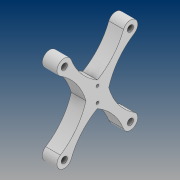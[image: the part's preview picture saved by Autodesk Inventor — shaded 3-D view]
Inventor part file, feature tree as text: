
AUTODESK INVENTOR PART (.ipt)
format: ipt  version: 2021 (Build 250183000, 183)  size: 144,384 bytes
history: native  units: mm
features: sketch x3, hole x2, extrude x1, projected_geometry x1
ambient origin geometry x8: Origin, YZ Plane, XZ Plane, XY Plane, X Axis, Y Axis, Z Axis, Center Point
bodies: Solid1 (feature_tree)
feature tree (7):
  extrude  "Extrusion1"  Depth=45.0mm
  hole  "Hole1"  [1 undecoded]
  hole  "Hole2"  [1 undecoded]
  sketch  "Sketch1"  dims[d0=55.0mm d1=45.0mm]
  sketch  "Sketch2"  dims[d2=10.0mm d3=15.0mm]
  projected_geometry  "Projected Loop1"
  sketch  "Sketch3"  dims[d4=41.0mm d5=10.0mm d6=0.0mm d7=4.2mm d8=6.0mm d9=4.0mm d10=2.0mm d11=90.0deg d12=8.0mm d13=20.594885mm d14=10.0mm d15=1.8mm d16=6.0mm d17=4.0mm d18=2.0mm d19=90.0deg d20=8.0mm d21=20.594885mm]
note: 2 required parameter values undecoded (feature->parameter linkage not recoverable at this tier; creation-order binding heuristic only, values carry confidence <= 0.55)
